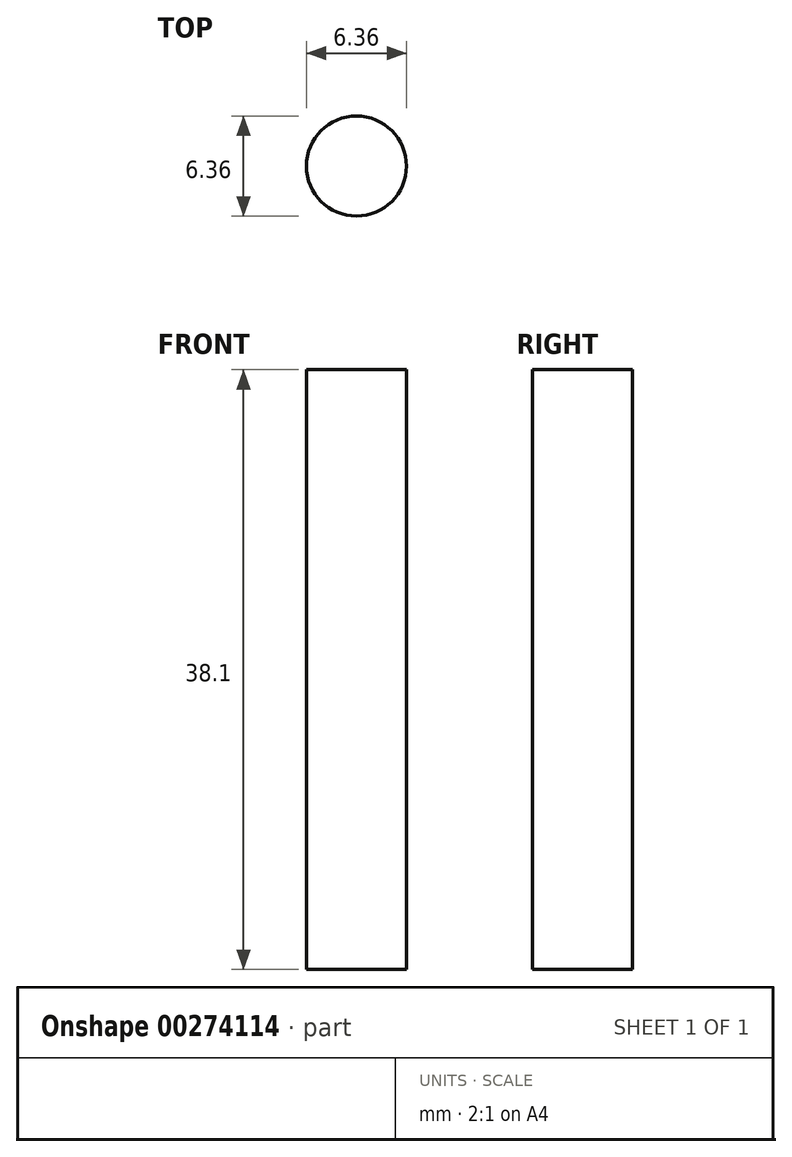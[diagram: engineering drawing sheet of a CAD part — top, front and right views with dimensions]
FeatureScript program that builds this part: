
annotation { "Feature Type Name" : "Feature", "Feature Type Description" : "" }
export const myFeature = defineFeature(function(context is Context, id is Id, definition is map)
    precondition{}
    {
        {
            var Q0;
            Q0=qCreatedBy(makeId("Top.planeOp"),FACE);
            var sketch = newSketch(context, id + "F0", { "sketchPlane" : qUnion([Q0])});
            skCircle(sketch, "E0", {"center": v(0, 0) * mm, "radius": 3.18 * mm});
            skSolve(sketch);
        }
        {
            var Q0;
            Q0=makeQuery(id+"F0.imprint","IMPRINT",FACE,{"disambiguationData":[TD([[makeQuery(id+"F0.imprint","IMPRINT",EDGE,{"derivedFrom":sQuery(id+"F0.wireOp",EDGE,"E0")}),1.0]])]});
            extrude(context, id + "F1", {"entities" : qUnion([Q0]), "depth" : 38.1 * mm});
        }
    });
